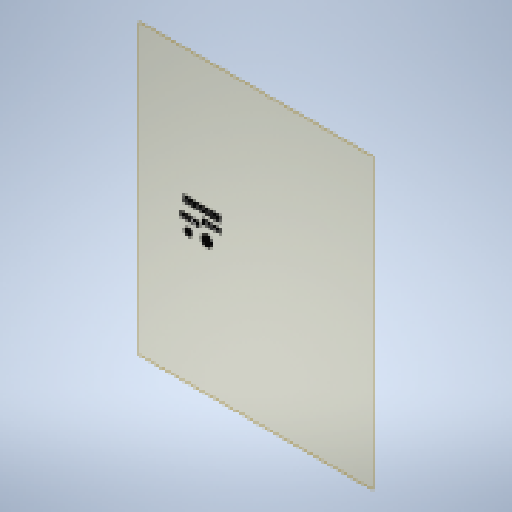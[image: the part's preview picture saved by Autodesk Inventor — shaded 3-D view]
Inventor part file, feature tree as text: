
AUTODESK INVENTOR PART (.ipt)
format: ipt  version: 2023 (Build 270158030, 158C)  size: 227,840 bytes
history: native  units: mm
features: other x9, sketch x4, plane x1, extrude x1
ambient origin geometry x8: Origin, YZ Plane, XZ Plane, XY Plane, X Axis, Y Axis, Z Axis, Center Point
bodies: Solid1 (feature_tree)
feature tree (15):
  plane  "Work Plane1"
  extrude  "Extrusion1"  Depth=12.0mm
  other  "Decal1"
  other  "Decal2"
  other  "Decal3"
  sketch  "Sketch1"  dims[d0=70.0mm d1=12.0mm]
  sketch  "Sketch2"  dims[d2=16.0mm]
  other  "Image1"
  sketch  "Sketch3"  dims[d3=20.0mm]
  other  "Image2"
  sketch  "Sketch4"  dims[d4=22.0mm d5=29.0mm d6=10.0mm d7=35.0mm d8=10.0mm d9=35.0mm d11=8.5mm d12=25.0mm d13=2.5mm d14=35.0mm d15=5.0mm d16=20.0mm d17=15.0mm d18=1.0mm d19=0.0mm d77=14.0mm d82=3.0mm d83=2.0mm d84=1.2mm d85=7.0mm d88=2.0mm d91=2.0mm d92=6.0mm d93=2.416667mm d95=4.5mm d96=2.0mm d97=2.0mm d98=4.916667mm]
  other  "Image3"
  other  "<userpath>\Documents\0004-inventor\Inventor_Projects\electronics-enclosure\enclosure.iam"
  other  "enclosure.iam"
  other  "door:1"
